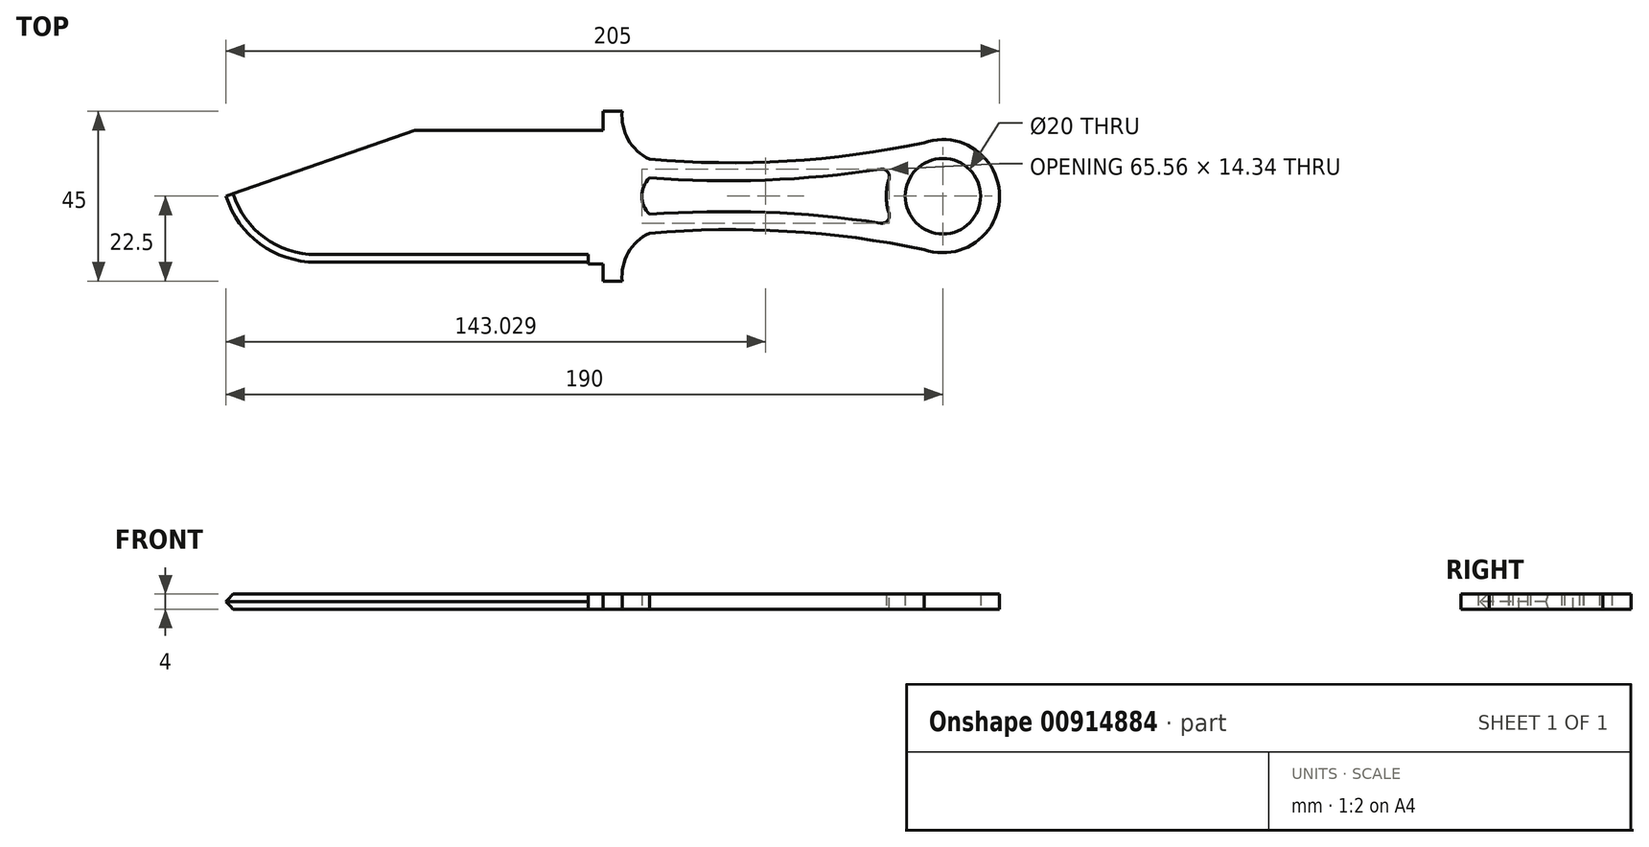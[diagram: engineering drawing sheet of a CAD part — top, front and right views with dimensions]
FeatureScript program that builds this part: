
annotation { "Feature Type Name" : "Feature", "Feature Type Description" : "" }
export const myFeature = defineFeature(function(context is Context, id is Id, definition is map)
    precondition{}
    {
        {
            var Q0;
            Q0=qCreatedBy(makeId("Top.planeOp"),FACE);
            var sketch = newSketch(context, id + "F0", { "sketchPlane" : qUnion([Q0])});
            skLineSegment(sketch, "E0.bottom", {"start": v(50, 17.5) * mm, "end": v(0, 17.5) * mm});
            skLineSegment(sketch, "E0.top", {"start": v(50, -17.5) * mm, "end": v(-26.15, -17.5) * mm});
            skPoint(sketch, "E0.middle", {"position": v(0, 0) * mm});
            skPoint(sketch, "E1", {"position": v(-50, 0) * mm});
            skLineSegment(sketch, "E2", {"start": v(-50, 0) * mm, "end": v(0, 17.5) * mm});
            skArc(sketch, "E3.trimOffspring", {"start": v(-50, 0) * mm, "mid": v(-40.94, -12.66) * mm, "end": v(-26.15, -17.5) * mm});
            skPoint(sketch, "E4.trimOffspring.end.orphan", {"position": v(-50, 17.5) * mm});
            skPoint(sketch, "E5.orphan", {"position": v(-50, -17.5) * mm});
            skLineSegment(sketch, "E6.bottom", {"start": v(50, 22.5) * mm, "end": v(55, 22.5) * mm});
            skLineSegment(sketch, "E6.top", {"start": v(50, -22.5) * mm, "end": v(55, -22.5) * mm});
            skLineSegment(sketch, "E6.left", {"start": v(50, 22.5) * mm, "end": v(50, 17.5) * mm});
            skArc(sketch, "E7", {"start": v(55, 22.5) * mm, "mid": v(56.6, 15.01) * mm, "end": v(62.2, 9.8) * mm});
            skLineSegment(sketch, "E8", {"start": v(62.2, -9.8) * mm, "end": v(62.2, 9.8) * mm, "construction": true});
            skArc(sketch, "E9", {"start": v(62.2, -9.8) * mm, "mid": v(56.6, -15.01) * mm, "end": v(55, -22.5) * mm});
            skArc(sketch, "E10", {"start": v(62.2, 9.8) * mm, "mid": v(98.76, 9.3) * mm, "end": v(135, 14.14) * mm});
            skArc(sketch, "E11", {"start": v(135, -14.14) * mm, "mid": v(98.76, -9.3) * mm, "end": v(62.2, -9.8) * mm});
            skArc(sketch, "E12.0", {"start": v(62.2, 4.83) * mm, "mid": v(60.25, 0) * mm, "end": v(62.2, -4.83) * mm});
            skArc(sketch, "E13", {"start": v(62.2, 4.83) * mm, "mid": v(94.76, 4.36) * mm, "end": v(127.15, 7.73) * mm});
            skArc(sketch, "E14", {"start": v(127.15, -7.73) * mm, "mid": v(94.76, -4.36) * mm, "end": v(62.2, -4.83) * mm});
            skLineSegment(sketch, "E15.trimOffspring", {"start": v(50, -17.5) * mm, "end": v(50, -22.5) * mm});
            skPoint(sketch, "E16.center.orphan", {"position": v(62.2, 0) * mm});
            skCircle(sketch, "E17.converted", {"center": v(140, 0) * mm, "radius": 10 * mm});
            skArc(sketch, "E18.converted", {"start": v(127.15, 7.73) * mm, "mid": v(125, 0) * mm, "end": v(127.15, -7.73) * mm});
            skPoint(sketch, "E19.orphan", {"position": v(137, 9.54) * mm});
            skPoint(sketch, "E20.orphan", {"position": v(137, -9.54) * mm});
            skArc(sketch, "E21.trimOffspring", {"start": v(135, -14.14) * mm, "mid": v(155, 0) * mm, "end": v(135, 14.14) * mm});
            skSolve(sketch);
        }
        {
            var Q0;
            Q0 = qSketchRegion(id + "F0", true);
            extrude(context, id + "F1", {"entities" : qUnion([Q0]), "depth" : 4 * mm, "offsetDistance" : 25 * mm});
        }
        {
            var Q0;
            Q0=makeQuery(id+"F1.opExtrude","SWEPT_EDGE",EDGE,{"disambiguationData":[OSD([sQuery(id+"F0.wireOp",EDGE,"E13"),sQuery(id+"F0.wireOp",EDGE,"E18.converted")])]});
            var Q1;
            Q1=makeQuery(id+"F1.opExtrude","SWEPT_EDGE",EDGE,{"disambiguationData":[OSD([sQuery(id+"F0.wireOp",EDGE,"E14"),sQuery(id+"F0.wireOp",EDGE,"E18.converted")])]});
            fillet(context, id + "F2", {"entities" : qUnion([Q0, Q1]), "radius" : 2 * mm, "tangentPropagation" : true, "allowEdgeOverflow" : false});
        }
        {
            var Q0;
            Q0=makeQuery(id+"F1.opExtrude","SWEPT_FACE",FACE,{"disambiguationData":[OSD([sQuery(id+"F0.wireOp",EDGE,"E0.top")])]});
            var sketch = newSketch(context, id + "F3", { "sketchPlane" : qUnion([Q0])});
            skLineSegment(sketch, "E22.bottom", {"start": v(50, 4) * mm, "end": v(46, 4) * mm});
            skLineSegment(sketch, "E22.top", {"start": v(50, 0) * mm, "end": v(46, 0) * mm});
            skLineSegment(sketch, "E22.left", {"start": v(50, 4) * mm, "end": v(50, 0) * mm});
            skLineSegment(sketch, "E22.right", {"start": v(46, 4) * mm, "end": v(46, 0) * mm});
            skSolve(sketch);
        }
        {
            var Q0;
            Q0 = qSketchRegion(id + "F3", true);
            extrude(context, id + "F4", {"entities" : qUnion([Q0]), "operationType" : NewBodyOperationType.ADD, "depth" : 0.5 * mm, "offsetDistance" : 25 * mm});
        }
        {
            var Q0;
            Q0=makeQuery(id+"F1.opExtrude","CAP_EDGE",EDGE,{"disambiguationData":[OSD([sQuery(id+"F0.wireOp",EDGE,"E0.top")])],"isStart":false});
            var Q1;
            Q1=makeQuery(id+"F1.opExtrude","CAP_EDGE",EDGE,{"disambiguationData":[OSD([sQuery(id+"F0.wireOp",EDGE,"E0.top")])],"isStart":true});
            chamfer(context, id + "F5", {"entities" : qUnion([Q0, Q1]), "width" : 2 * mm, "tangentPropagation" : true});
        }
    });
